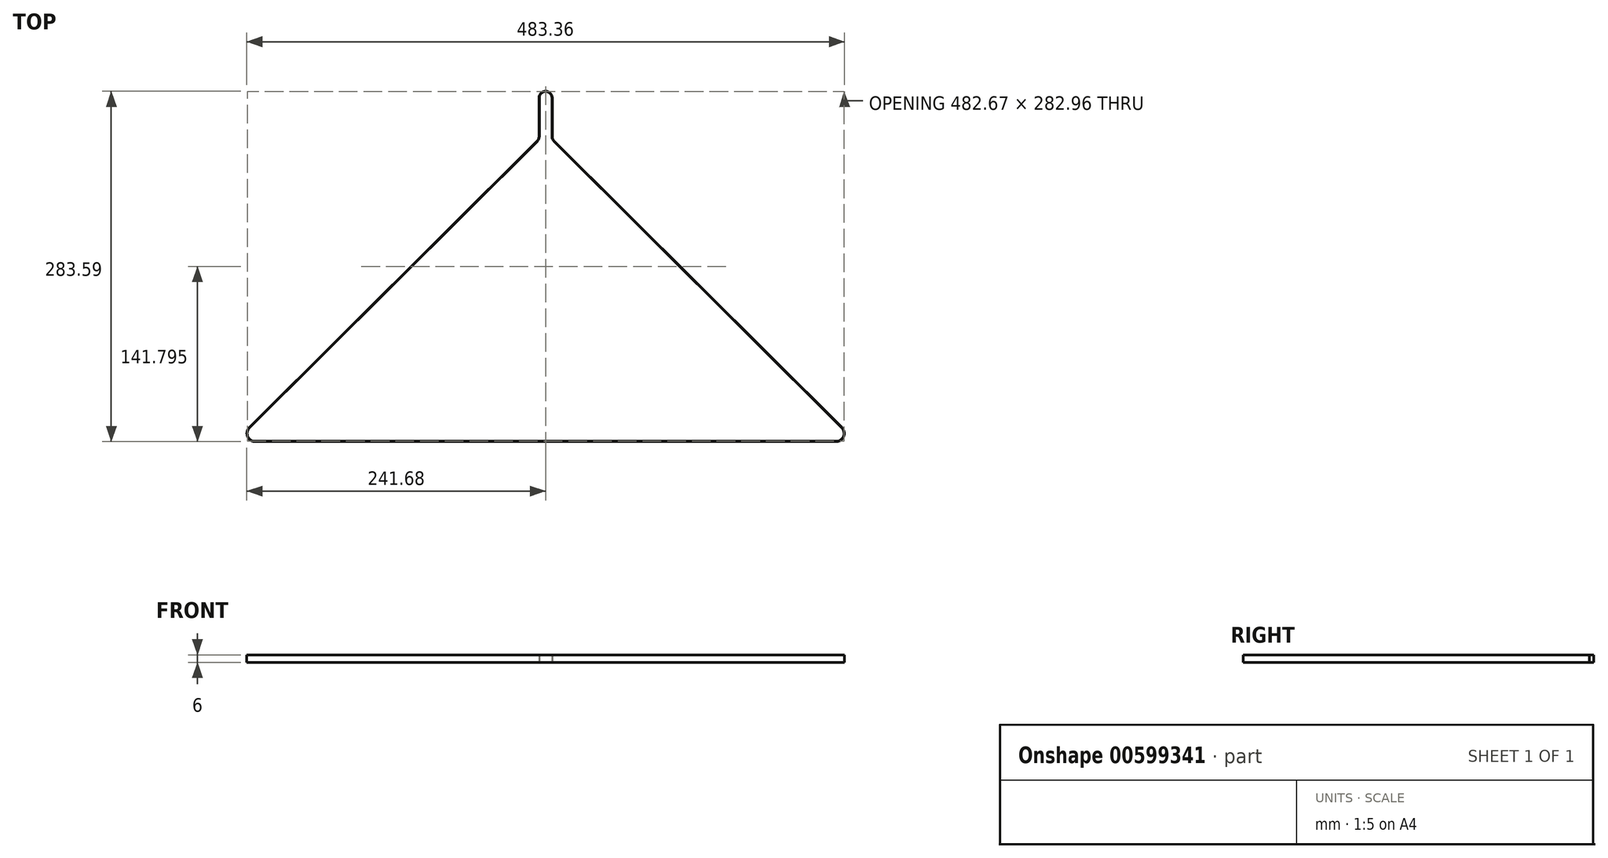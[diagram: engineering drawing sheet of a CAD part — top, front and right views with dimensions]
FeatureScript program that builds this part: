
annotation { "Feature Type Name" : "Feature", "Feature Type Description" : "" }
export const myFeature = defineFeature(function(context is Context, id is Id, definition is map)
    precondition{}
    {
        {
            var Q0;
            Q0=qCreatedBy(makeId("Top.planeOp"),FACE);
            var sketch = newSketch(context, id + "F0", { "sketchPlane" : qUnion([Q0])});
            skLineSegment(sketch, "E0", {"start": v(-235, 0) * mm, "end": v(235, 0) * mm, "construction": true});
            skLineSegment(sketch, "E1", {"start": v(235, 0) * mm, "end": v(0, 271.5) * mm, "construction": true});
            skLineSegment(sketch, "E2", {"start": v(0, 271.5) * mm, "end": v(-235, 0) * mm, "construction": true});
            skArc(sketch, "E3", {"start": v(-230.83, 4.81) * mm, "mid": v(-240.96, 2.22) * mm, "end": v(-235, -6.37) * mm});
            skArc(sketch, "E4", {"start": v(235, -6.37) * mm, "mid": v(240.88, -2.43) * mm, "end": v(239.5, 4.5) * mm});
            skLineSegment(sketch, "E5", {"start": v(-5.04, 273.48) * mm, "end": v(-5.1, 273.4) * mm});
            skLineSegment(sketch, "E6", {"start": v(5.04, 273.48) * mm, "end": v(5.1, 273.4) * mm});
            skLineSegment(sketch, "E7", {"start": v(235, -6.36) * mm, "end": v(-235, -6.37) * mm});
            skPoint(sketch, "E8.orphan", {"position": v(0, 279.25) * mm});
            skPoint(sketch, "E9.orphan", {"position": v(243.44, 0) * mm});
            skArc(sketch, "E10", {"start": v(-230.63, 5.05) * mm, "mid": v(-241.26, 2.33) * mm, "end": v(-235, -6.68) * mm});
            skArc(sketch, "E11", {"start": v(235, -6.68) * mm, "mid": v(241.17, -2.55) * mm, "end": v(239.71, 4.73) * mm});
            skLineSegment(sketch, "E12", {"start": v(-235, -6.68) * mm, "end": v(235, -6.68) * mm});
            skLineSegment(sketch, "E13.trimOffspring", {"start": v(0, 298.25) * mm, "end": v(0.15, 298.42) * mm});
            skPoint(sketch, "E14.orphan", {"position": v(243.86, 0) * mm});
            skArc(sketch, "E15", {"start": v(-6.9, 236.64) * mm, "mid": v(-5.8, 238.3) * mm, "end": v(-5.4, 240.25) * mm});
            skArc(sketch, "E16", {"start": v(5.41, 240.25) * mm, "mid": v(5.8, 238.3) * mm, "end": v(6.9, 236.64) * mm});
            skArc(sketch, "E17.converted", {"start": v(5.4, 271.5) * mm, "mid": v(0, 276.91) * mm, "end": v(-5.4, 271.5) * mm});
            skArc(sketch, "E18.converted", {"start": v(5.1, 271.5) * mm, "mid": v(0, 276.6) * mm, "end": v(-5.1, 271.5) * mm});
            skArc(sketch, "E19", {"start": v(-6.69, 236.42) * mm, "mid": v(-5.5, 238.17) * mm, "end": v(-5.1, 240.25) * mm});
            skArc(sketch, "E20", {"start": v(5.1, 240.25) * mm, "mid": v(5.5, 238.17) * mm, "end": v(6.69, 236.42) * mm});
            skLineSegment(sketch, "E21", {"start": v(-5.1, 273.4) * mm, "end": v(-5.1, 273.32) * mm});
            skLineSegment(sketch, "E22", {"start": v(5.1, 273.4) * mm, "end": v(5.1, 273.32) * mm});
            skLineSegment(sketch, "E23", {"start": v(5.4, 271.5) * mm, "end": v(5.41, 240.25) * mm});
            skLineSegment(sketch, "E24.trimOffspring", {"start": v(-5.4, 271.5) * mm, "end": v(-5.4, 240.25) * mm});
            skLineSegment(sketch, "E25.trimOffspring", {"start": v(-5.1, 271.5) * mm, "end": v(-5.1, 240.25) * mm});
            skLineSegment(sketch, "E26.trimOffspring", {"start": v(5.1, 271.5) * mm, "end": v(5.1, 240.25) * mm});
            skPoint(sketch, "E27.orphan", {"position": v(4.09, 275.05) * mm});
            skPoint(sketch, "E28.orphan", {"position": v(5.1, 275.05) * mm});
            skLineSegment(sketch, "E29", {"start": v(-239.71, 4.73) * mm, "end": v(-6.9, 236.64) * mm});
            skPoint(sketch, "E30.orphan", {"position": v(-244.47, 0) * mm});
            skLineSegment(sketch, "E31", {"start": v(-244.47, -0.44) * mm, "end": v(-6.69, 236.42) * mm});
            skLineSegment(sketch, "E32", {"start": v(6.9, 236.64) * mm, "end": v(239.71, 4.73) * mm});
            skLineSegment(sketch, "E33.trimOffspring", {"start": v(6.69, 236.42) * mm, "end": v(239.5, 4.5) * mm});
            skSolve(sketch);
        }
        {
            var Q0;
            Q0=qSketchRegion(id+"F0",true);
            extrude(context, id + "F1", {"entities" : qUnion([Q0]), "depth" : 6 * mm, "offsetDistance" : 25 * mm});
        }
    });
